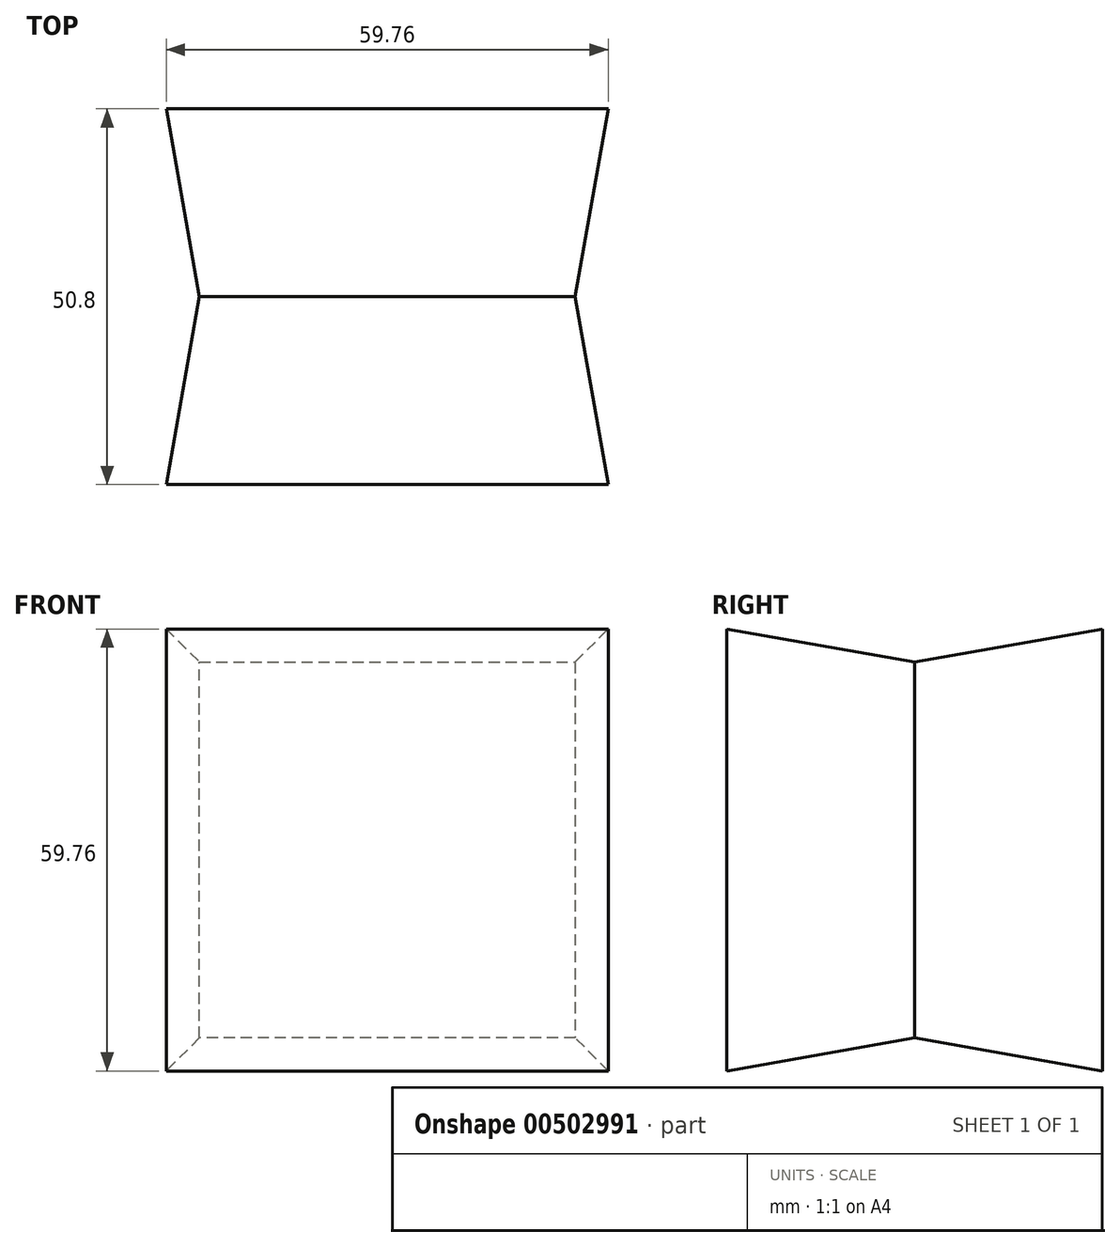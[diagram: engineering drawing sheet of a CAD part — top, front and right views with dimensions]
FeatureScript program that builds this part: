
annotation { "Feature Type Name" : "Feature", "Feature Type Description" : "" }
export const myFeature = defineFeature(function(context is Context, id is Id, definition is map)
    precondition{}
    {
        {
            var Q0;
            Q0=qCreatedBy(makeId("Front.planeOp"),FACE);
            var sketch = newSketch(context, id + "F0", { "sketchPlane" : qUnion([Q0])});
            skLineSegment(sketch, "E0.bottom", {"start": v(25.4, 25.4) * mm, "end": v(-25.4, 25.4) * mm});
            skLineSegment(sketch, "E0.top", {"start": v(25.4, -25.4) * mm, "end": v(-25.4, -25.4) * mm});
            skLineSegment(sketch, "E0.left", {"start": v(25.4, 25.4) * mm, "end": v(25.4, -25.4) * mm});
            skLineSegment(sketch, "E0.right", {"start": v(-25.4, 25.4) * mm, "end": v(-25.4, -25.4) * mm});
            skPoint(sketch, "E0.middle", {"position": v(0, 0) * mm});
            skSolve(sketch);
        }
        {
            var Q0;
            Q0 = qSketchRegion(id + "F0", true);
            extrude(context, id + "F1", {"entities" : qUnion([Q0]), "endBound" : BoundingType.SYMMETRIC, "depth" : 50.8 * mm, "hasDraft" : true, "draftAngle" : 10 * degree});
        }
    });
